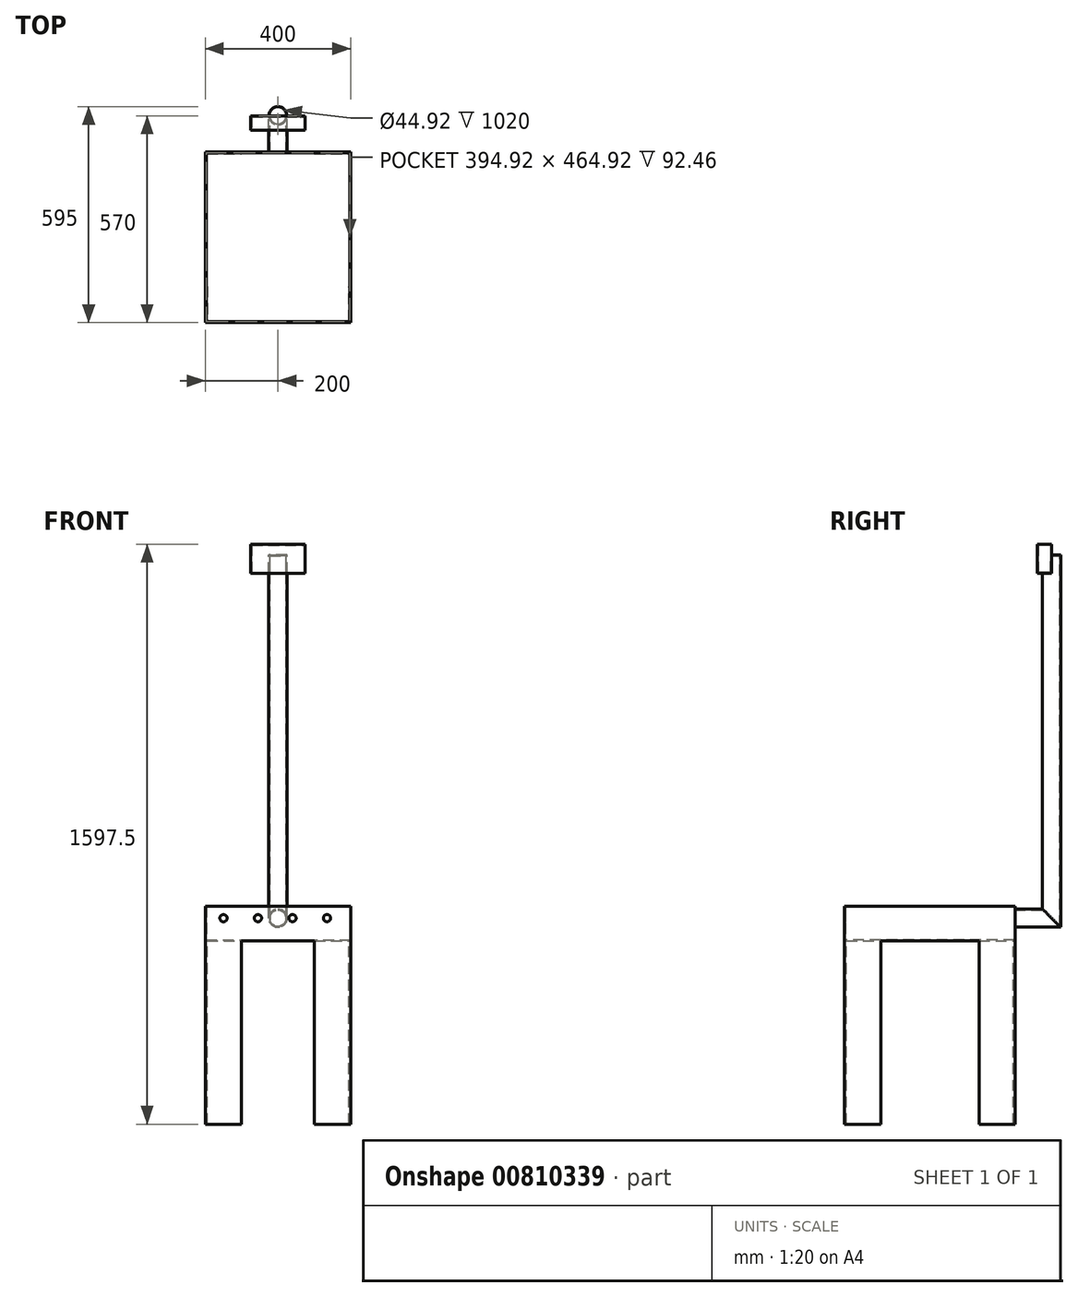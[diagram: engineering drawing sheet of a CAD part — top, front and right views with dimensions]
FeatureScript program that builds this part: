
annotation { "Feature Type Name" : "Feature", "Feature Type Description" : "" }
export const myFeature = defineFeature(function(context is Context, id is Id, definition is map)
    precondition{}
    {
        {
            var Q0;
            Q0=qCreatedBy(makeId("Top.planeOp"),FACE);
            var sketch = newSketch(context, id + "F0", { "sketchPlane" : qUnion([Q0])});
            skLineSegment(sketch, "E0.bottom", {"start": v(-200, 235) * mm, "end": v(200, 235) * mm});
            skLineSegment(sketch, "E0.top", {"start": v(-200, -235) * mm, "end": v(200, -235) * mm});
            skLineSegment(sketch, "E0.left", {"start": v(-200, 235) * mm, "end": v(-200, -235) * mm});
            skLineSegment(sketch, "E0.right", {"start": v(200, 235) * mm, "end": v(200, -235) * mm});
            skLineSegment(sketch, "E1", {"start": v(-880.74, 0) * mm, "end": v(1003.35, 0) * mm, "construction": true});
            skLineSegment(sketch, "E2", {"start": v(0, 696.83) * mm, "end": v(0, -451.6) * mm, "construction": true});
            skSolve(sketch);
        }
        {
            var Q0;
            Q0 = qSketchRegion(id + "F0", true);
            extrude(context, id + "F1", {"entities" : qUnion([Q0]), "depth" : 125 * mm, "offsetDistance" : 25.4 * mm});
        }
        {
            var Q0;
            Q0=makeQuery(id+"F1.opExtrude","SWEPT_FACE",FACE,{"disambiguationData":[OSD([sQuery(id+"F0.wireOp",EDGE,"E0.left")])]});
            cPlane(context, id + "F2", {"entities" : qUnion([Q0]), "cplaneType" : CPlaneType.OFFSET, "offset" : 200 * mm, "oppositeDirection" : true, "width" : 152.4 * mm, "height" : 152.4 * mm});
        }
        {
            var Q0;
            Q0=qCreatedBy(id+"F2.planeOp",FACE);
            var sketch = newSketch(context, id + "F3", { "sketchPlane" : qUnion([Q0])});
            skLineSegment(sketch, "E3", {"start": v(-235, 62.5) * mm, "end": v(-335, 62.5) * mm});
            skLineSegment(sketch, "E4", {"start": v(-335, 62.5) * mm, "end": v(-335, 1062.5) * mm});
            skSolve(sketch);
        }
        {
            var Q0;
            Q0=makeQuery(id+"F1.opExtrude","SWEPT_FACE",FACE,{"disambiguationData":[OSD([sQuery(id+"F0.wireOp",EDGE,"E0.bottom")])]});
            var sketch = newSketch(context, id + "F4", { "sketchPlane" : qUnion([Q0])});
            skCircle(sketch, "E5", {"center": v(0, 62.5) * mm, "radius": 25 * mm});
            skSolve(sketch);
        }
        {
            var Q0;
            Q0=makeQuery(id+"F4.imprint","IMPRINT",FACE,{"disambiguationData":[TD([[makeQuery(id+"F4.imprint","IMPRINT",EDGE,{"derivedFrom":sQuery(id+"F4.wireOp",EDGE,"E5")}),1.0]])]});
            var Q1;
            Q1=sQuery(id+"F3.wireOp",EDGE,"E3");
            var Q2;
            Q2=sQuery(id+"F3.wireOp",EDGE,"E4");
            sweep(context, id + "F5", {"operationType" : NewBodyOperationType.ADD, "profiles" : qUnion([Q0]), "path" : qUnion([Q1, Q2])});
        }
        {
            var Q0;
            Q0=makeQuery(id+"F5.opSweep","CAP_FACE",FACE,{"disambiguationData":[OSD([sQuery(id+"F3.wireOp",VERTEX,"E4.end"),sQuery(id+"F4.wireOp",EDGE,"E5")])],"isStart":false});
            var sketch = newSketch(context, id + "F6", { "sketchPlane" : qUnion([Q0])});
            skLineSegment(sketch, "E6", {"start": v(0, 425.15) * mm, "end": v(0, 261.48) * mm, "construction": true});
            skLineSegment(sketch, "E7", {"start": v(0, 335) * mm, "end": v(166.7, 335) * mm, "construction": true});
            skLineSegment(sketch, "E8", {"start": v(0, 335) * mm, "end": v(-125.48, 335) * mm, "construction": true});
            skLineSegment(sketch, "E9.bottom", {"start": v(-38.2, 335) * mm, "end": v(39.4, 335) * mm});
            skLineSegment(sketch, "E9.top", {"start": v(-38.2, 299.06) * mm, "end": v(39.4, 299.06) * mm});
            skLineSegment(sketch, "E9.left", {"start": v(-38.2, 335) * mm, "end": v(-38.2, 299.06) * mm});
            skLineSegment(sketch, "E9.right", {"start": v(39.4, 335) * mm, "end": v(39.4, 299.06) * mm});
            skSolve(sketch);
        }
        {
            var Q0;
            Q0 = qSketchRegion(id + "F6", true);
            extrude(context, id + "F7", {"entities" : qUnion([Q0]), "operationType" : NewBodyOperationType.REMOVE, "oppositeDirection" : true, "depth" : 50 * mm, "offsetDistance" : 25.4 * mm});
        }
        {
            var Q0;
            Q0=makeQuery(id+"F7.boolean.opBoolean","COPY",FACE,{"derivedFrom":makeQuery(id+"F7.opExtrude","CAP_FACE",FACE,{"disambiguationData":[OSD([sQuery(id+"F6.wireOp",EDGE,"E9.bottom"),sQuery(id+"F6.wireOp",EDGE,"E9.top"),sQuery(id+"F6.wireOp",EDGE,"E9.left"),sQuery(id+"F6.wireOp",EDGE,"E9.right")])],"isStart":false})});
            var sketch = newSketch(context, id + "F8", { "sketchPlane" : qUnion([Q0])});
            skLineSegment(sketch, "E10.bottom", {"start": v(-75, 335) * mm, "end": v(75, 335) * mm});
            skLineSegment(sketch, "E10.top", {"start": v(-75, 295) * mm, "end": v(75, 295) * mm});
            skLineSegment(sketch, "E10.left", {"start": v(-75, 335) * mm, "end": v(-75, 295) * mm});
            skLineSegment(sketch, "E10.right", {"start": v(75, 335) * mm, "end": v(75, 295) * mm});
            skLineSegment(sketch, "E11", {"start": v(0, 335) * mm, "end": v(0, 261.08) * mm, "construction": true});
            skPoint(sketch, "E11.endSnap0", {"position": v(0, 310) * mm});
            skPoint(sketch, "E12.startSnap0", {"position": v(-75, 315) * mm});
            skPoint(sketch, "E12.endSnap0", {"position": v(75, 315) * mm});
            skSolve(sketch);
        }
        {
            var Q0;
            Q0 = qSketchRegion(id + "F8", true);
            extrude(context, id + "F9", {"entities" : qUnion([Q0]), "operationType" : NewBodyOperationType.ADD, "depth" : 80 * mm, "offsetDistance" : 25.4 * mm});
        }
        {
            var Q0;
            Q0=makeQuery(id+"F1.opExtrude","CAP_FACE",FACE,{"disambiguationData":[OSD([sQuery(id+"F0.wireOp",EDGE,"E0.bottom"),sQuery(id+"F0.wireOp",EDGE,"E0.top"),sQuery(id+"F0.wireOp",EDGE,"E0.left"),sQuery(id+"F0.wireOp",EDGE,"E0.right")])],"isStart":false});
            shell(context, id + "F10", {"entities" : qUnion([Q0]), "thickness" : 2.54 * mm});
        }
        {
            var Q0;
            Q0=makeQuery(id+"F1.opExtrude","SWEPT_FACE",FACE,{"disambiguationData":[OSD([sQuery(id+"F0.wireOp",EDGE,"E0.top")])]});
            var sketch = newSketch(context, id + "F11", { "sketchPlane" : qUnion([Q0])});
            skLineSegment(sketch, "E13", {"start": v(-316.66, 62.5) * mm, "end": v(279.08, 62.5) * mm, "construction": true});
            skPoint(sketch, "E13.startSnap0", {"position": v(-200, 62.5) * mm});
            skCircle(sketch, "E14", {"center": v(-150, 62.5) * mm, "radius": 10 * mm});
            skCircle(sketch, "E15.1.0.0", {"center": v(-55, 62.5) * mm, "radius": 10 * mm});
            skCircle(sketch, "E15.2.0.0", {"center": v(40, 62.5) * mm, "radius": 10 * mm});
            skCircle(sketch, "E15.3.0.0", {"center": v(135, 62.5) * mm, "radius": 10 * mm});
            skLineSegment(sketch, "E15.direction1", {"start": v(-150, 62.5) * mm, "end": v(-55, 62.5) * mm, "construction": true});
            skSolve(sketch);
        }
        {
            var Q0;
            Q0 = qSketchRegion(id + "F11", true);
            extrude(context, id + "F12", {"entities" : qUnion([Q0]), "operationType" : NewBodyOperationType.REMOVE, "endBound" : BoundingType.THROUGH_ALL, "oppositeDirection" : true, "depth" : 25.4 * mm, "offsetDistance" : 25.4 * mm});
        }
        {
            var Q0;
            Q0=makeQuery(id+"F1.opExtrude","CAP_FACE",FACE,{"disambiguationData":[OSD([sQuery(id+"F0.wireOp",EDGE,"E0.bottom"),sQuery(id+"F0.wireOp",EDGE,"E0.top"),sQuery(id+"F0.wireOp",EDGE,"E0.left"),sQuery(id+"F0.wireOp",EDGE,"E0.right")])],"isStart":true});
            var sketch = newSketch(context, id + "F13", { "sketchPlane" : qUnion([Q0])});
            skLineSegment(sketch, "E16", {"start": v(-200, 135) * mm, "end": v(-200, 235) * mm});
            skLineSegment(sketch, "E17", {"start": v(-200, 235) * mm, "end": v(-100, 235) * mm});
            skLineSegment(sketch, "E18", {"start": v(-200, 135) * mm, "end": v(-195, 135) * mm});
            skLineSegment(sketch, "E19", {"start": v(-195, 135) * mm, "end": v(-195, 230) * mm});
            skLineSegment(sketch, "E20", {"start": v(-195, 230) * mm, "end": v(-100, 230) * mm});
            skLineSegment(sketch, "E21", {"start": v(-100, 230) * mm, "end": v(-100, 235) * mm});
            skLineSegment(sketch, "E22", {"start": v(-200, -135) * mm, "end": v(-200, -235) * mm});
            skLineSegment(sketch, "E23", {"start": v(-200, -235) * mm, "end": v(-100, -235) * mm});
            skLineSegment(sketch, "E24", {"start": v(-200, -135) * mm, "end": v(-195, -135) * mm});
            skLineSegment(sketch, "E25", {"start": v(-195, -135) * mm, "end": v(-195, -230) * mm});
            skLineSegment(sketch, "E26", {"start": v(-195, -230) * mm, "end": v(-100, -230) * mm});
            skLineSegment(sketch, "E27", {"start": v(-100, -230) * mm, "end": v(-100, -235) * mm});
            skLineSegment(sketch, "E28", {"start": v(200, -135) * mm, "end": v(200, -235) * mm});
            skLineSegment(sketch, "E29", {"start": v(200, -235) * mm, "end": v(100, -235) * mm});
            skLineSegment(sketch, "E30", {"start": v(100, -235) * mm, "end": v(100, -230) * mm});
            skLineSegment(sketch, "E31", {"start": v(100, -230) * mm, "end": v(195, -230) * mm});
            skLineSegment(sketch, "E32", {"start": v(195, -230) * mm, "end": v(195, -135) * mm});
            skLineSegment(sketch, "E33", {"start": v(195, -135) * mm, "end": v(200, -135) * mm});
            skLineSegment(sketch, "E34", {"start": v(100, 235) * mm, "end": v(200, 235) * mm});
            skLineSegment(sketch, "E35", {"start": v(200, 235) * mm, "end": v(200, 135) * mm});
            skLineSegment(sketch, "E36", {"start": v(100, 235) * mm, "end": v(100, 230) * mm});
            skLineSegment(sketch, "E37", {"start": v(100, 230) * mm, "end": v(195, 230) * mm});
            skLineSegment(sketch, "E38", {"start": v(195, 230) * mm, "end": v(195, 135) * mm});
            skLineSegment(sketch, "E39", {"start": v(195, 135) * mm, "end": v(200, 135) * mm});
            skSolve(sketch);
        }
        {
            var Q0;
            Q0 = qSketchRegion(id + "F13", true);
            extrude(context, id + "F14", {"entities" : qUnion([Q0]), "operationType" : NewBodyOperationType.ADD, "depth" : 505 * mm, "offsetDistance" : 25.4 * mm});
        }
        {
            var Q0;
            Q0=makeQuery(id+"F14.boolean.opBoolean","MERGE",FACE,{"derivedFrom":[makeQuery(id+"F1.opExtrude","SWEPT_FACE",FACE,{"disambiguationData":[OSD([sQuery(id+"F0.wireOp",EDGE,"E0.left")])]}),makeQuery(id+"F14.opExtrude","SWEPT_FACE",FACE,{"disambiguationData":[OSD([sQuery(id+"F13.wireOp",EDGE,"E16")])]}),makeQuery(id+"F14.opExtrude","SWEPT_FACE",FACE,{"disambiguationData":[OSD([sQuery(id+"F13.wireOp",EDGE,"E22")])]})]});
            var sketch = newSketch(context, id + "F15", { "sketchPlane" : qUnion([Q0])});
            skLineSegment(sketch, "E40.bottom", {"start": v(-260.27, 125) * mm, "end": v(1238.55, 125) * mm});
            skLineSegment(sketch, "E40.top", {"start": v(-260.27, 95) * mm, "end": v(1238.55, 95) * mm});
            skLineSegment(sketch, "E40.left", {"start": v(-260.27, 125) * mm, "end": v(-260.27, 95) * mm});
            skLineSegment(sketch, "E40.right", {"start": v(1238.55, 125) * mm, "end": v(1238.55, 95) * mm});
            skSolve(sketch);
        }
        {
            var Q0;
            Q0 = qSketchRegion(id + "F15", true);
            extrude(context, id + "F16", {"entities" : qUnion([Q0]), "operationType" : NewBodyOperationType.REMOVE, "endBound" : BoundingType.THROUGH_ALL, "oppositeDirection" : true, "depth" : 25.4 * mm, "offsetDistance" : 25.4 * mm});
        }
    });
